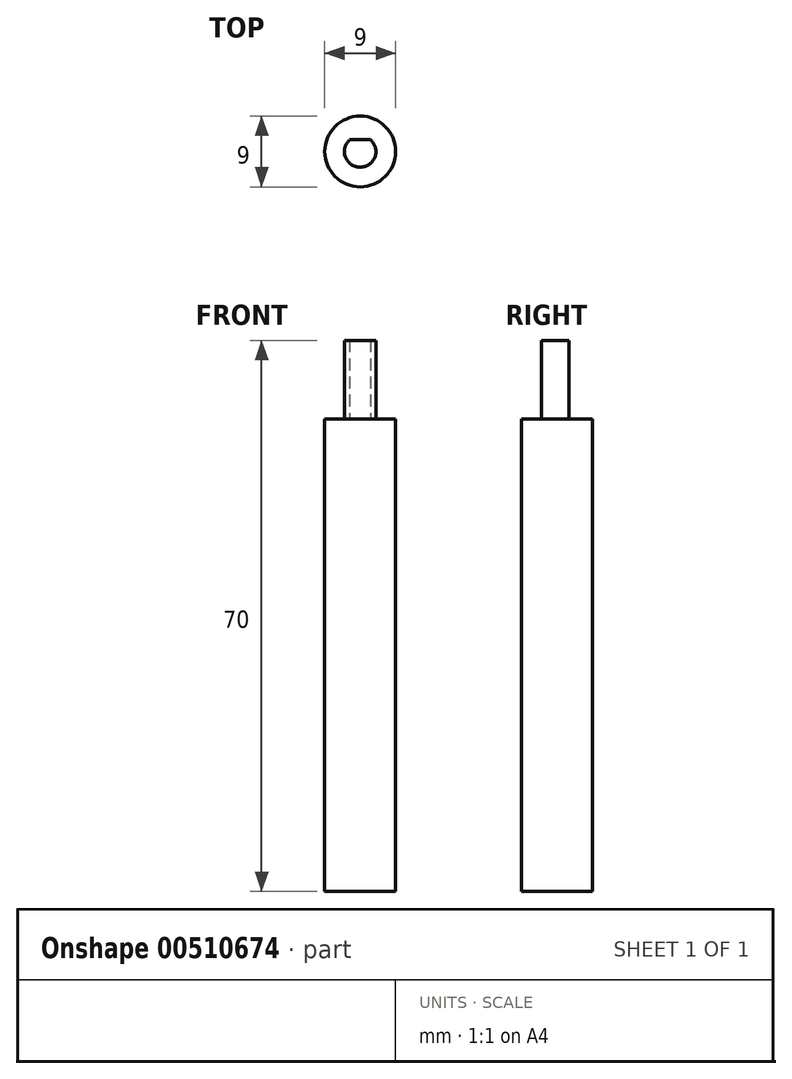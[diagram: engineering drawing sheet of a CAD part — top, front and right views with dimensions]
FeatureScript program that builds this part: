
annotation { "Feature Type Name" : "Feature", "Feature Type Description" : "" }
export const myFeature = defineFeature(function(context is Context, id is Id, definition is map)
    precondition{}
    {
        {
            var Q0;
            Q0=qCreatedBy(makeId("Top.planeOp"),FACE);
            var sketch = newSketch(context, id + "F0", { "sketchPlane" : qUnion([Q0])});
            skCircle(sketch, "E0", {"center": v(0, 0) * mm, "radius": 4.5 * mm});
            skArc(sketch, "E1", {"start": v(-1.32, 1.5) * mm, "mid": v(0, -2) * mm, "end": v(1.32, 1.5) * mm});
            skLineSegment(sketch, "E2", {"start": v(10.28, 0) * mm, "end": v(-10.17, 0) * mm, "construction": true});
            skLineSegment(sketch, "E3", {"start": v(-1.32, 1.5) * mm, "end": v(1.32, 1.5) * mm});
            skSolve(sketch);
        }
        {
            var Q0;
            Q0=makeQuery(id+"F0.imprint","IMPRINT",FACE,{"disambiguationData":[TD([[makeQuery(id+"F0.imprint","IMPRINT",EDGE,{"derivedFrom":sQuery(id+"F0.wireOp",EDGE,"E0")}),1.0]])]});
            var Q1;
            Q1=makeQuery(id+"F0.imprint","IMPRINT",FACE,{"disambiguationData":[TD([[makeQuery(id+"F0.imprint","IMPRINT",EDGE,{"derivedFrom":sQuery(id+"F0.wireOp",EDGE,"E1")}),1.0]])]});
            extrude(context, id + "F1", {"entities" : qUnion([Q0, Q1]), "oppositeDirection" : true, "depth" : 60 * mm});
        }
        {
            var Q0;
            Q0=makeQuery(id+"F0.imprint","IMPRINT",FACE,{"disambiguationData":[TD([[makeQuery(id+"F0.imprint","IMPRINT",EDGE,{"derivedFrom":sQuery(id+"F0.wireOp",EDGE,"E1")}),1.0]])]});
            extrude(context, id + "F2", {"entities" : qUnion([Q0]), "depth" : 10 * mm});
        }
    });
